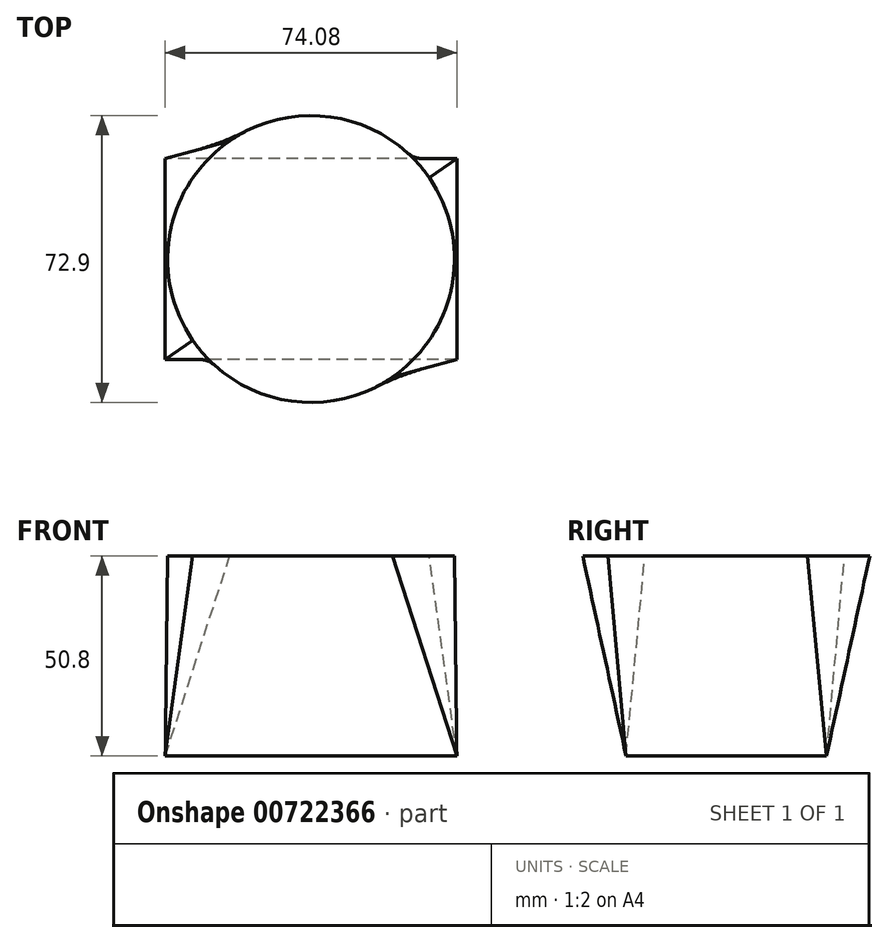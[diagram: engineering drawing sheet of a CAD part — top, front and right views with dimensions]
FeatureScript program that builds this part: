
annotation { "Feature Type Name" : "Feature", "Feature Type Description" : "" }
export const myFeature = defineFeature(function(context is Context, id is Id, definition is map)
    precondition{}
    {
        {
            var Q0;
            Q0=qCreatedBy(makeId("Top.planeOp"),FACE);
            var sketch = newSketch(context, id + "F0", { "sketchPlane" : qUnion([Q0])});
            skLineSegment(sketch, "E0.bottom", {"start": v(37.04, 25.47) * mm, "end": v(-37.04, 25.47) * mm});
            skLineSegment(sketch, "E0.top", {"start": v(37.04, -25.47) * mm, "end": v(-37.04, -25.47) * mm});
            skLineSegment(sketch, "E0.left", {"start": v(37.04, 25.47) * mm, "end": v(37.04, -25.47) * mm});
            skLineSegment(sketch, "E0.right", {"start": v(-37.04, 25.47) * mm, "end": v(-37.04, -25.47) * mm});
            skPoint(sketch, "E0.middle", {"position": v(0, 0) * mm});
            skSolve(sketch);
        }
        {
            var Q0;
            Q0=qCreatedBy(makeId("Top.planeOp"),FACE);
            cPlane(context, id + "F1", {"entities" : qUnion([Q0]), "cplaneType" : CPlaneType.OFFSET, "offset" : 50.8 * mm, "width" : 152.4 * mm, "height" : 152.4 * mm});
        }
        {
            var Q0;
            Q0=qCreatedBy(id+"F1.planeOp",FACE);
            var sketch = newSketch(context, id + "F2", { "sketchPlane" : qUnion([Q0])});
            skCircle(sketch, "E1", {"center": v(0, 0) * mm, "radius": 36.45 * mm});
            skSolve(sketch);
        }
        {
            var Q0;
            Q0=makeQuery(id+"F0.imprint","IMPRINT",FACE,{"disambiguationData":[TD([[makeQuery(id+"F0.imprint","IMPRINT",EDGE,{"derivedFrom":sQuery(id+"F0.wireOp",EDGE,"E0.bottom")}),1.0]])]});
            var Q1;
            Q1=makeQuery(id+"F2.imprint","IMPRINT",FACE,{"disambiguationData":[TD([[makeQuery(id+"F2.imprint","IMPRINT",EDGE,{"derivedFrom":sQuery(id+"F2.wireOp",EDGE,"E1")}),1.0]])]});
            loft(context, id + "F3", {"sheetProfilesArray" : [{ "sheetProfileEntities" : qUnion([Q0]) }, { "sheetProfileEntities" : qUnion([Q1]) }]});
        }
    });
